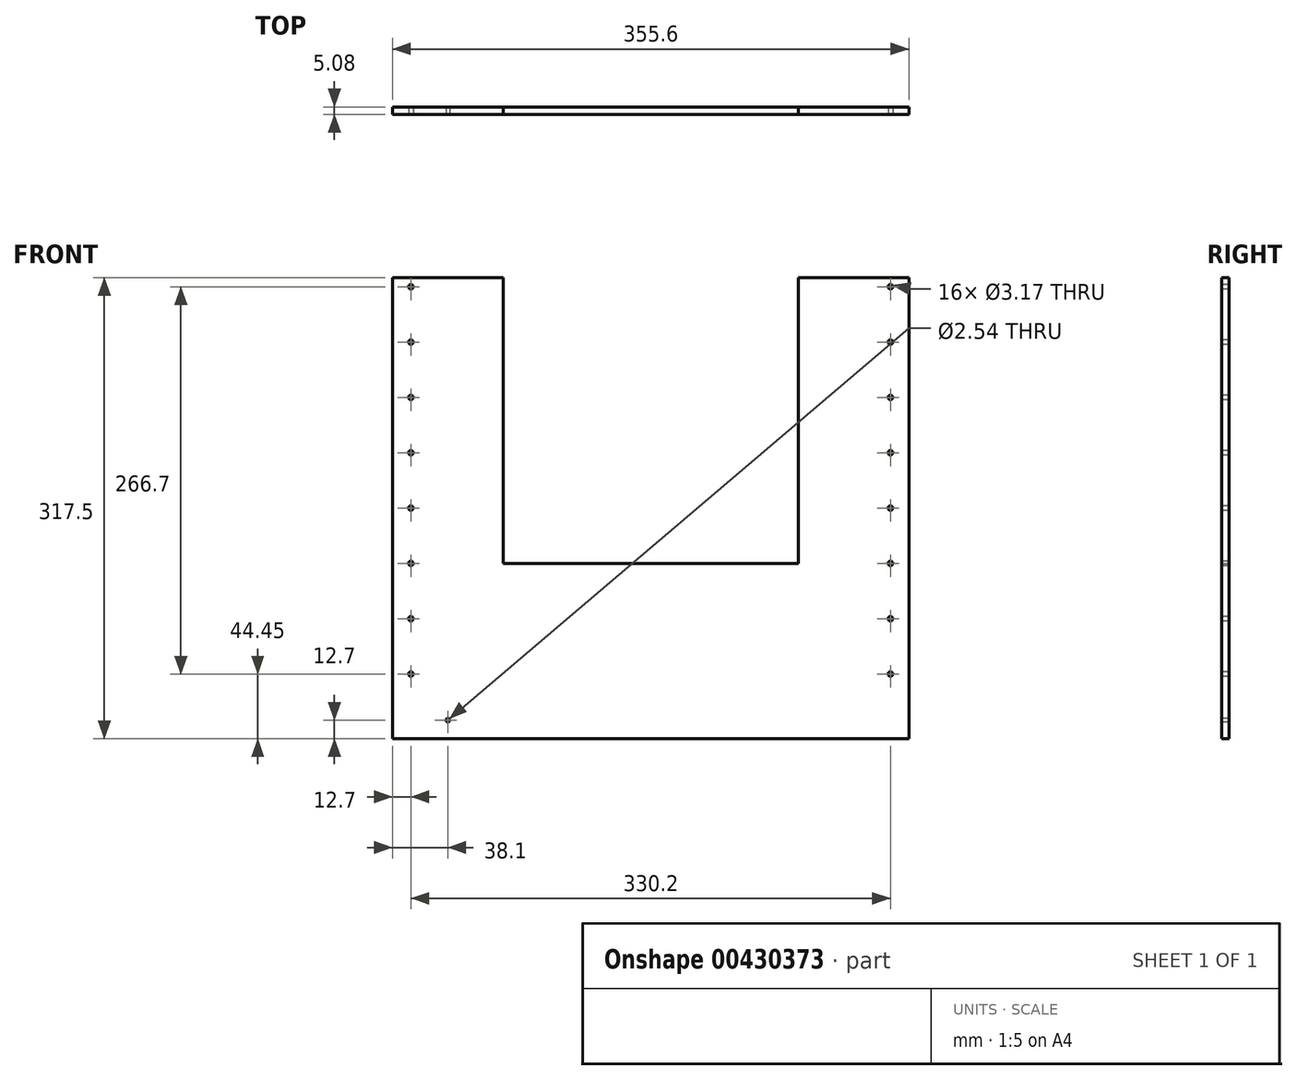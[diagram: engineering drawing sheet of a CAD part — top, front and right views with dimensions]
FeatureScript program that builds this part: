
annotation { "Feature Type Name" : "Feature", "Feature Type Description" : "" }
export const myFeature = defineFeature(function(context is Context, id is Id, definition is map)
    precondition{}
    {
        {
            var Q0;
            Q0=qCreatedBy(makeId("Front.planeOp"),FACE);
            var sketch = newSketch(context, id + "F0", { "sketchPlane" : qUnion([Q0])});
            skLineSegment(sketch, "E0", {"start": v(0, 0) * mm, "end": v(-355.6, 0) * mm});
            skLineSegment(sketch, "E1", {"start": v(-355.6, 0) * mm, "end": v(-355.6, 317.5) * mm});
            skLineSegment(sketch, "E2", {"start": v(-355.6, 317.5) * mm, "end": v(-279.4, 317.5) * mm});
            skLineSegment(sketch, "E3", {"start": v(-279.4, 120.65) * mm, "end": v(-279.4, 317.5) * mm});
            skLineSegment(sketch, "E4", {"start": v(0, 0) * mm, "end": v(0, 317.5) * mm});
            skLineSegment(sketch, "E5", {"start": v(0, 317.5) * mm, "end": v(-76.2, 317.5) * mm});
            skLineSegment(sketch, "E6", {"start": v(-76.2, 317.5) * mm, "end": v(-76.2, 120.65) * mm});
            skLineSegment(sketch, "E7", {"start": v(-76.2, 120.65) * mm, "end": v(-279.4, 120.65) * mm});
            skSolve(sketch);
        }
        {
            var Q0;
            Q0=makeQuery(id+"F0.imprint","IMPRINT",FACE,{"disambiguationData":[TD([[makeQuery(id+"F0.imprint","IMPRINT",EDGE,{"derivedFrom":sQuery(id+"F0.wireOp",EDGE,"E0")}),-1.0]])]});
            extrude(context, id + "F1", {"entities" : qUnion([Q0]), "depth" : 5.08 * mm});
        }
        {
            var Q0;
            Q0=makeQuery(id+"F1.opExtrude","CAP_FACE",FACE,{"disambiguationData":[OSD([sQuery(id+"F0.wireOp",EDGE,"E0"),sQuery(id+"F0.wireOp",EDGE,"E1"),sQuery(id+"F0.wireOp",EDGE,"E2"),sQuery(id+"F0.wireOp",EDGE,"E3"),sQuery(id+"F0.wireOp",EDGE,"E4"),sQuery(id+"F0.wireOp",EDGE,"E5"),sQuery(id+"F0.wireOp",EDGE,"E6"),sQuery(id+"F0.wireOp",EDGE,"E7")])],"isStart":false});
            var sketch = newSketch(context, id + "F2", { "sketchPlane" : qUnion([Q0])});
            skLineSegment(sketch, "E8", {"start": v(-177.8, 120.65) * mm, "end": v(-177.8, 0) * mm});
            skLineSegment(sketch, "E9", {"start": v(-355.6, 0) * mm, "end": v(-317.5, 0) * mm});
            skLineSegment(sketch, "E10", {"start": v(-317.5, 0) * mm, "end": v(-317.5, 12.7) * mm});
            skCircle(sketch, "E11", {"center": v(-317.5, 12.7) * mm, "radius": 1.27 * mm});
            skSolve(sketch);
        }
        {
            var Q0;
            Q0=makeQuery(id+"F2.imprint","IMPRINT",FACE,{"disambiguationData":[TD([[makeQuery(id+"F2.imprint","IMPRINT",EDGE,{"derivedFrom":sQuery(id+"F2.wireOp",EDGE,"E11")}),1.0]])]});
            extrude(context, id + "F3", {"entities" : qUnion([Q0]), "operationType" : NewBodyOperationType.REMOVE, "oppositeDirection" : true, "depth" : 25.4 * mm});
        }
        {
            var Q0;
            Q0=makeQuery(id+"F1.opExtrude","CAP_FACE",FACE,{"disambiguationData":[OSD([sQuery(id+"F0.wireOp",EDGE,"E0"),sQuery(id+"F0.wireOp",EDGE,"E1"),sQuery(id+"F0.wireOp",EDGE,"E2"),sQuery(id+"F0.wireOp",EDGE,"E3"),sQuery(id+"F0.wireOp",EDGE,"E4"),sQuery(id+"F0.wireOp",EDGE,"E5"),sQuery(id+"F0.wireOp",EDGE,"E6"),sQuery(id+"F0.wireOp",EDGE,"E7")])],"isStart":false});
            var sketch = newSketch(context, id + "F4", { "sketchPlane" : qUnion([Q0])});
            skLineSegment(sketch, "E12", {"start": v(0, 0) * mm, "end": v(-38.1, 0) * mm});
            skLineSegment(sketch, "E13", {"start": v(-38.1, 0) * mm, "end": v(-38.1, 12.7) * mm});
            skLineSegment(sketch, "E14", {"start": v(-355.6, 317.5) * mm, "end": v(-342.9, 317.5) * mm});
            skLineSegment(sketch, "E15", {"start": v(0, 317.5) * mm, "end": v(-12.7, 317.5) * mm});
            skLineSegment(sketch, "E16", {"start": v(-342.9, 317.5) * mm, "end": v(-342.9, 311.15) * mm});
            skCircle(sketch, "E17", {"center": v(-342.9, 311.15) * mm, "radius": 1.59 * mm});
            skCircle(sketch, "E18.0.1.0", {"center": v(-342.9, 273.05) * mm, "radius": 1.59 * mm});
            skCircle(sketch, "E18.0.2.0", {"center": v(-342.9, 234.95) * mm, "radius": 1.59 * mm});
            skCircle(sketch, "E18.0.3.0", {"center": v(-342.9, 196.85) * mm, "radius": 1.59 * mm});
            skCircle(sketch, "E18.0.4.0", {"center": v(-342.9, 158.75) * mm, "radius": 1.59 * mm});
            skCircle(sketch, "E18.0.5.0", {"center": v(-342.9, 120.65) * mm, "radius": 1.59 * mm});
            skCircle(sketch, "E18.0.6.0", {"center": v(-342.9, 82.55) * mm, "radius": 1.59 * mm});
            skCircle(sketch, "E18.0.7.0", {"center": v(-342.9, 44.45) * mm, "radius": 1.59 * mm});
            skLineSegment(sketch, "E18.direction1", {"start": v(-342.9, 311.15) * mm, "end": v(-317.5, 311.15) * mm, "construction": true});
            skLineSegment(sketch, "E18.direction2", {"start": v(-342.9, 311.15) * mm, "end": v(-342.9, 273.05) * mm, "construction": true});
            skLineSegment(sketch, "E19", {"start": v(-12.7, 317.5) * mm, "end": v(-12.7, 311.15) * mm});
            skCircle(sketch, "E20", {"center": v(-12.7, 311.15) * mm, "radius": 1.59 * mm});
            skCircle(sketch, "E21.0.1.0", {"center": v(-12.7, 273.05) * mm, "radius": 1.59 * mm});
            skCircle(sketch, "E21.0.2.0", {"center": v(-12.7, 234.95) * mm, "radius": 1.59 * mm});
            skCircle(sketch, "E21.0.3.0", {"center": v(-12.7, 196.85) * mm, "radius": 1.59 * mm});
            skCircle(sketch, "E21.0.4.0", {"center": v(-12.7, 158.75) * mm, "radius": 1.59 * mm});
            skCircle(sketch, "E21.0.5.0", {"center": v(-12.7, 120.65) * mm, "radius": 1.59 * mm});
            skCircle(sketch, "E21.0.6.0", {"center": v(-12.7, 82.55) * mm, "radius": 1.59 * mm});
            skCircle(sketch, "E21.0.7.0", {"center": v(-12.7, 44.45) * mm, "radius": 1.59 * mm});
            skLineSegment(sketch, "E21.direction1", {"start": v(-12.7, 311.15) * mm, "end": v(12.7, 311.15) * mm, "construction": true});
            skLineSegment(sketch, "E21.direction2", {"start": v(-12.7, 311.15) * mm, "end": v(-12.7, 273.05) * mm, "construction": true});
            skSolve(sketch);
        }
        {
            var Q0;
            Q0=makeQuery(id+"F4.imprint","IMPRINT",FACE,{"disambiguationData":[TD([[makeQuery(id+"F4.imprint","IMPRINT",EDGE,{"derivedFrom":sQuery(id+"F4.wireOp",EDGE,"E17")}),1.0]])]});
            var Q1;
            Q1=makeQuery(id+"F4.imprint","IMPRINT",FACE,{"disambiguationData":[TD([[makeQuery(id+"F4.imprint","IMPRINT",EDGE,{"derivedFrom":sQuery(id+"F4.wireOp",EDGE,"E18.0.1.0")}),1.0]])]});
            var Q2;
            Q2=makeQuery(id+"F4.imprint","IMPRINT",FACE,{"disambiguationData":[TD([[makeQuery(id+"F4.imprint","IMPRINT",EDGE,{"derivedFrom":sQuery(id+"F4.wireOp",EDGE,"E18.0.2.0")}),1.0]])]});
            var Q3;
            Q3=makeQuery(id+"F4.imprint","IMPRINT",FACE,{"disambiguationData":[TD([[makeQuery(id+"F4.imprint","IMPRINT",EDGE,{"derivedFrom":sQuery(id+"F4.wireOp",EDGE,"E18.0.3.0")}),1.0]])]});
            var Q4;
            Q4=makeQuery(id+"F4.imprint","IMPRINT",FACE,{"disambiguationData":[TD([[makeQuery(id+"F4.imprint","IMPRINT",EDGE,{"derivedFrom":sQuery(id+"F4.wireOp",EDGE,"E18.0.4.0")}),1.0]])]});
            var Q5;
            Q5=makeQuery(id+"F4.imprint","IMPRINT",FACE,{"disambiguationData":[TD([[makeQuery(id+"F4.imprint","IMPRINT",EDGE,{"derivedFrom":sQuery(id+"F4.wireOp",EDGE,"E18.0.5.0")}),1.0]])]});
            var Q6;
            Q6=makeQuery(id+"F4.imprint","IMPRINT",FACE,{"disambiguationData":[TD([[makeQuery(id+"F4.imprint","IMPRINT",EDGE,{"derivedFrom":sQuery(id+"F4.wireOp",EDGE,"E18.0.6.0")}),1.0]])]});
            var Q7;
            Q7=makeQuery(id+"F4.imprint","IMPRINT",FACE,{"disambiguationData":[TD([[makeQuery(id+"F4.imprint","IMPRINT",EDGE,{"derivedFrom":sQuery(id+"F4.wireOp",EDGE,"E18.0.7.0")}),1.0]])]});
            var Q8;
            Q8=makeQuery(id+"F4.imprint","IMPRINT",FACE,{"disambiguationData":[TD([[makeQuery(id+"F4.imprint","IMPRINT",EDGE,{"derivedFrom":sQuery(id+"F4.wireOp",EDGE,"E21.0.7.0")}),1.0]])]});
            var Q9;
            Q9=makeQuery(id+"F4.imprint","IMPRINT",FACE,{"disambiguationData":[TD([[makeQuery(id+"F4.imprint","IMPRINT",EDGE,{"derivedFrom":sQuery(id+"F4.wireOp",EDGE,"E21.0.6.0")}),1.0]])]});
            var Q10;
            Q10=makeQuery(id+"F4.imprint","IMPRINT",FACE,{"disambiguationData":[TD([[makeQuery(id+"F4.imprint","IMPRINT",EDGE,{"derivedFrom":sQuery(id+"F4.wireOp",EDGE,"E21.0.5.0")}),1.0]])]});
            var Q11;
            Q11=makeQuery(id+"F4.imprint","IMPRINT",FACE,{"disambiguationData":[TD([[makeQuery(id+"F4.imprint","IMPRINT",EDGE,{"derivedFrom":sQuery(id+"F4.wireOp",EDGE,"E21.0.4.0")}),1.0]])]});
            var Q12;
            Q12=makeQuery(id+"F4.imprint","IMPRINT",FACE,{"disambiguationData":[TD([[makeQuery(id+"F4.imprint","IMPRINT",EDGE,{"derivedFrom":sQuery(id+"F4.wireOp",EDGE,"E21.0.3.0")}),1.0]])]});
            var Q13;
            Q13=makeQuery(id+"F4.imprint","IMPRINT",FACE,{"disambiguationData":[TD([[makeQuery(id+"F4.imprint","IMPRINT",EDGE,{"derivedFrom":sQuery(id+"F4.wireOp",EDGE,"E21.0.2.0")}),1.0]])]});
            var Q14;
            Q14=makeQuery(id+"F4.imprint","IMPRINT",FACE,{"disambiguationData":[TD([[makeQuery(id+"F4.imprint","IMPRINT",EDGE,{"derivedFrom":sQuery(id+"F4.wireOp",EDGE,"E21.0.1.0")}),1.0]])]});
            var Q15;
            Q15=makeQuery(id+"F4.imprint","IMPRINT",FACE,{"disambiguationData":[TD([[makeQuery(id+"F4.imprint","IMPRINT",EDGE,{"derivedFrom":sQuery(id+"F4.wireOp",EDGE,"E20")}),1.0]])]});
            extrude(context, id + "F5", {"entities" : qUnion([Q0, Q1, Q2, Q3, Q4, Q5, Q6, Q7, Q8, Q9, Q10, Q11, Q12, Q13, Q14, Q15]), "operationType" : NewBodyOperationType.REMOVE, "oppositeDirection" : true, "depth" : 25.4 * mm});
        }
    });
